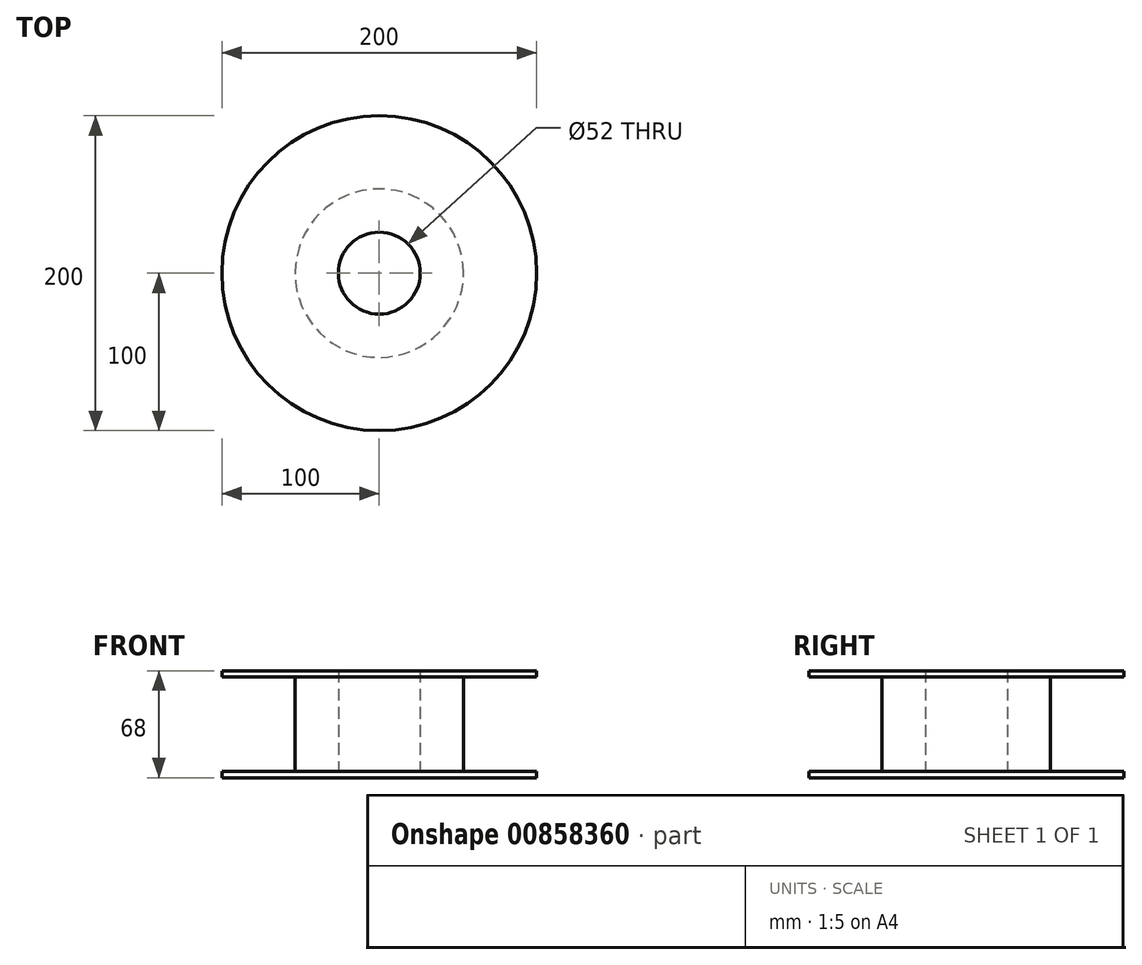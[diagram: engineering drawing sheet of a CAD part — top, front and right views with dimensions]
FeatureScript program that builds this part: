
annotation { "Feature Type Name" : "Feature", "Feature Type Description" : "" }
export const myFeature = defineFeature(function(context is Context, id is Id, definition is map)
    precondition{}
    {
        {
            var Q0;
            Q0=qCreatedBy(makeId("Front.planeOp"),FACE);
            var sketch = newSketch(context, id + "F0", { "sketchPlane" : qUnion([Q0])});
            skLineSegment(sketch, "E0", {"start": v(-100, 34) * mm, "end": v(-100, 30) * mm});
            skLineSegment(sketch, "E1", {"start": v(-100, 30) * mm, "end": v(-53.5, 30) * mm});
            skLineSegment(sketch, "E2", {"start": v(-53.5, 30) * mm, "end": v(-53.5, -30) * mm});
            skLineSegment(sketch, "E3", {"start": v(-53.5, -30) * mm, "end": v(-100, -30) * mm});
            skLineSegment(sketch, "E4", {"start": v(-100, -30) * mm, "end": v(-100, -34) * mm});
            skLineSegment(sketch, "E5", {"start": v(-100, -34) * mm, "end": v(-26, -34) * mm});
            skLineSegment(sketch, "E6", {"start": v(-100, 34) * mm, "end": v(-26, 34) * mm});
            skLineSegment(sketch, "E7", {"start": v(-26, 34) * mm, "end": v(-26, -34) * mm});
            skLineSegment(sketch, "E8", {"start": v(0, -36.61) * mm, "end": v(0, 31.36) * mm, "construction": true});
            skSolve(sketch);
        }
        {
            var Q0;
            Q0=makeQuery(id+"F0.imprint","IMPRINT",FACE,{"disambiguationData":[TD([[makeQuery(id+"F0.imprint","IMPRINT",EDGE,{"derivedFrom":sQuery(id+"F0.wireOp",EDGE,"E0")}),1.0]])]});
            var Q1;
            Q1=qConstructionFilter(qBodyType(qCreatedBy(id+"F0",EDGE),BodyType.WIRE),ConstructionObject.NO);
            var Q2;
            Q2=sQuery(id+"F0.wireOp",EDGE,"E8");
            revolve(context, id + "F1", {"surfaceOperationType" : NewSurfaceOperationType.NEW, "entities" : qUnion([Q0]), "surfaceEntities" : qUnion([Q1]), "axis" : qUnion([Q2]), "revolveType" : RevolveType.FULL});
        }
    });
